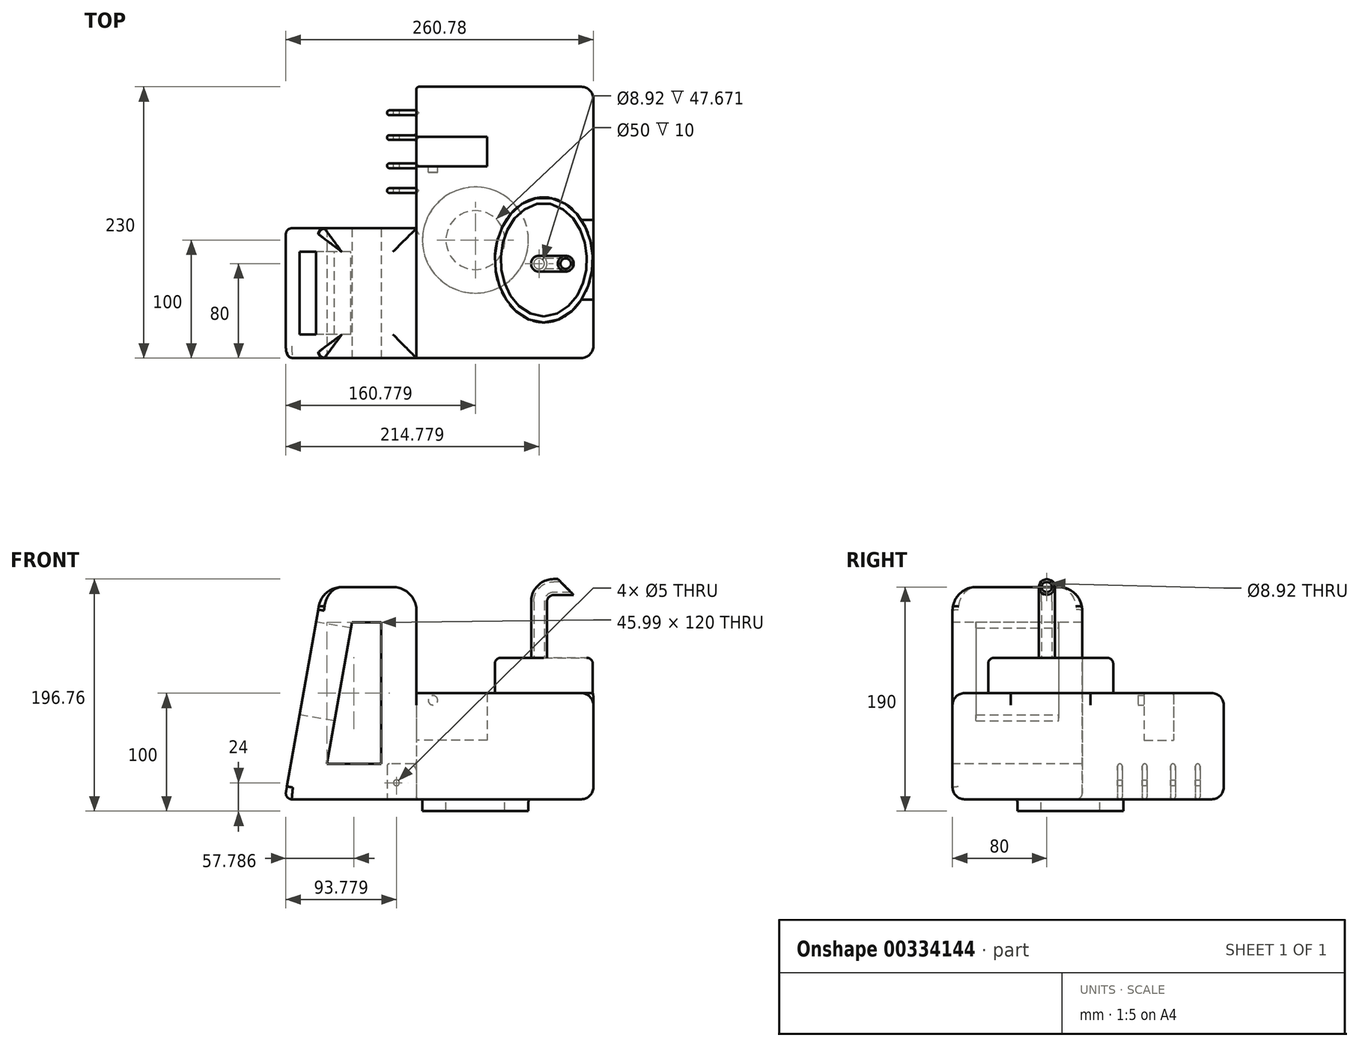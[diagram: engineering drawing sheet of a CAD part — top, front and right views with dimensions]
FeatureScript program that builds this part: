
annotation { "Feature Type Name" : "Feature", "Feature Type Description" : "" }
export const myFeature = defineFeature(function(context is Context, id is Id, definition is map)
    precondition{}
    {
        {
            var Q0;
            Q0=qCreatedBy(makeId("Front.planeOp"),FACE);
            var sketch = newSketch(context, id + "F0", { "sketchPlane" : qUnion([Q0])});
            skLineSegment(sketch, "E0", {"start": v(0, 0) * mm, "end": v(31.74, 180) * mm});
            skLineSegment(sketch, "E1", {"start": v(31.74, 180) * mm, "end": v(111.74, 180) * mm});
            skLineSegment(sketch, "E2", {"start": v(111.74, 180) * mm, "end": v(111.74, 0) * mm});
            skLineSegment(sketch, "E3", {"start": v(111.74, 0) * mm, "end": v(0, 0) * mm});
            skLineSegment(sketch, "E4", {"start": v(111.74, 90) * mm, "end": v(261.74, 90) * mm});
            skLineSegment(sketch, "E5", {"start": v(261.74, 90) * mm, "end": v(261.74, 0) * mm});
            skLineSegment(sketch, "E6", {"start": v(261.74, 0) * mm, "end": v(111.74, 0) * mm});
            skSolve(sketch);
        }
        {
            var Q0;
            {var subQ2=sQuery(id+"F0.wireOp",EDGE,"E4");Q0=makeQuery(id+"F0.imprint","IMPRINT",FACE,{"disambiguationData":[TD([[makeQuery(id+"F0.imprint","IMPRINT",EDGE,{"derivedFrom":subQ2}),-1.0]])]});}
            extrude(context, id + "F1", {"entities" : qUnion([Q0]), "oppositeDirection" : true, "depth" : 230 * mm});
        }
        {
            var Q0;
            Q0=makeQuery(id+"F0.imprint","IMPRINT",FACE,{"disambiguationData":[TD([[makeQuery(id+"F0.imprint","IMPRINT",EDGE,{"derivedFrom":sQuery(id+"F0.wireOp",EDGE,"E0")}),-1.0]])]});
            extrude(context, id + "F2", {"entities" : qUnion([Q0]), "operationType" : NewBodyOperationType.ADD, "oppositeDirection" : true, "depth" : 110 * mm});
        }
        {
            var Q0;
            Q0=makeQuery(id+"F2.boolean.opBoolean","MERGE",FACE,{"derivedFrom":[makeQuery(id+"F1.opExtrude","SWEPT_FACE",FACE,{"disambiguationData":[OSD([sQuery(id+"F0.wireOp",EDGE,"E6")])]}),makeQuery(id+"F2.opExtrude","SWEPT_FACE",FACE,{"disambiguationData":[OSD([sQuery(id+"F0.wireOp",EDGE,"E3")])]})]});
            var sketch = newSketch(context, id + "F3", { "sketchPlane" : qUnion([Q0])});
            skCircle(sketch, "E7", {"center": v(161.74, -100) * mm, "radius": 45 * mm});
            skCircle(sketch, "E8", {"center": v(161.74, -100) * mm, "radius": 25 * mm});
            skSolve(sketch);
        }
        {
            var Q0;
            Q0 = qSketchRegion(id + "F3", true);
            extrude(context, id + "F4", {"entities" : qUnion([Q0]), "operationType" : NewBodyOperationType.ADD, "depth" : 10 * mm});
        }
        {
            var Q0;
            Q0=makeQuery(id+"F0.imprint","IMPRINT",FACE,{"disambiguationData":[TD([[makeQuery(id+"F0.imprint","IMPRINT",EDGE,{"derivedFrom":sQuery(id+"F0.wireOp",EDGE,"E0")}),-1.0]])]});
            var sketch = newSketch(context, id + "F5", { "sketchPlane" : qUnion([Q0])});
            skLineSegment(sketch, "E9.0", {"start": v(81.74, 50) * mm, "end": v(81.74, 150) * mm});
            skLineSegment(sketch, "E9.1", {"start": v(81.74, 30) * mm, "end": v(81.74, 50) * mm});
            skLineSegment(sketch, "E9.2", {"start": v(81.74, 150) * mm, "end": v(56.91, 150) * mm});
            skLineSegment(sketch, "E9.3", {"start": v(56.91, 150) * mm, "end": v(35.75, 30) * mm});
            skLineSegment(sketch, "E9.4", {"start": v(35.75, 30) * mm, "end": v(81.74, 30) * mm});
            skSolve(sketch);
        }
        {
            var Q0;
            Q0 = qSketchRegion(id + "F5", true);
            extrude(context, id + "F6", {"entities" : qUnion([Q0]), "operationType" : NewBodyOperationType.REMOVE, "endBound" : BoundingType.THROUGH_ALL, "oppositeDirection" : true, "depth" : 25 * mm});
        }
        {
            var Q0;
            Q0=makeQuery(id+"F1.opExtrude","SWEPT_FACE",FACE,{"disambiguationData":[OSD([sQuery(id+"F0.wireOp",EDGE,"E2")])]});
            var sketch = newSketch(context, id + "F7", { "sketchPlane" : qUnion([Q0])});
            skLineSegment(sketch, "E10.bottom", {"start": v(-140, 30) * mm, "end": v(-144, 30) * mm});
            skLineSegment(sketch, "E10.top", {"start": v(-140, 0) * mm, "end": v(-144, 0) * mm});
            skLineSegment(sketch, "E10.left", {"start": v(-140, 30) * mm, "end": v(-140, 0) * mm});
            skLineSegment(sketch, "E10.right", {"start": v(-210, 30) * mm, "end": v(-210, 0) * mm});
            skPoint(sketch, "E10.middle", {"position": v(-175, 15) * mm});
            skLineSegment(sketch, "E11", {"start": v(-185, 30) * mm, "end": v(-185, 0) * mm});
            skLineSegment(sketch, "E12", {"start": v(-165, 30) * mm, "end": v(-165, 0) * mm});
            skLineSegment(sketch, "E13", {"start": v(-175, 98.41) * mm, "end": v(-175, -73.6) * mm, "construction": true});
            skLineSegment(sketch, "E14.trimOffspring", {"start": v(-185, 30) * mm, "end": v(-189, 30) * mm});
            skLineSegment(sketch, "E15.trimOffspring", {"start": v(-185, 0) * mm, "end": v(-189, 0) * mm});
            skPoint(sketch, "E16.centerSnap0", {"position": v(-197.5, 30) * mm});
            skPoint(sketch, "E16.centerSnap1", {"position": v(-210, 15) * mm});
            skLineSegment(sketch, "E17", {"start": v(-206, 30) * mm, "end": v(-206, 0) * mm});
            skLineSegment(sketch, "E18", {"start": v(-189, 30) * mm, "end": v(-189, 0) * mm});
            skLineSegment(sketch, "E19.MirrorCS", {"start": v(-161, 30) * mm, "end": v(-161, 0) * mm});
            skLineSegment(sketch, "E20.MirrorCS", {"start": v(-144, 30) * mm, "end": v(-144, 0) * mm});
            skLineSegment(sketch, "E21.trimOffspring", {"start": v(-206, 30) * mm, "end": v(-210, 30) * mm});
            skLineSegment(sketch, "E22.trimOffspring", {"start": v(-206, 0) * mm, "end": v(-210, 0) * mm});
            skLineSegment(sketch, "E23.trimOffspring", {"start": v(-161, 30) * mm, "end": v(-165, 30) * mm});
            skLineSegment(sketch, "E24.trimOffspring", {"start": v(-161, 0) * mm, "end": v(-165, 0) * mm});
            skSolve(sketch);
        }
        {
            var Q0;
            Q0 = qSketchRegion(id + "F7", true);
            extrude(context, id + "F8", {"entities" : qUnion([Q0]), "operationType" : NewBodyOperationType.ADD, "depth" : 25 * mm});
        }
        {
            var Q0;
            {var subQ2=sQuery(id+"F0.wireOp",EDGE,"E4");var subQ3=sQuery(id+"F0.wireOp",EDGE,"E2");Q0=makeQuery(id+"F8.boolean.opBoolean","SPLIT",FACE,{"disambiguationData":[TD([makeQuery(id+"F1.opExtrude","SWEPT_FACE",FACE,{"disambiguationData":[OSD([subQ2])]})])],"derivedFrom":makeQuery(id+"F1.opExtrude","SWEPT_FACE",FACE,{"disambiguationData":[OSD([subQ3])]})});}
            var sketch = newSketch(context, id + "F9", { "sketchPlane" : qUnion([Q0])});
            skLineSegment(sketch, "E25.top", {"start": v(-162.5, 50) * mm, "end": v(-187.5, 50) * mm});
            skLineSegment(sketch, "E25.left", {"start": v(-162.5, 90) * mm, "end": v(-162.5, 50) * mm});
            skLineSegment(sketch, "E25.right", {"start": v(-187.5, 90) * mm, "end": v(-187.5, 50) * mm});
            skPoint(sketch, "E25.middle", {"position": v(-175, 55) * mm});
            skPoint(sketch, "E26.orphan", {"position": v(-187.5, 60) * mm});
            skPoint(sketch, "E27.orphan", {"position": v(-162.5, 60) * mm});
            skLineSegment(sketch, "E28.0", {"start": v(-187.5, 90) * mm, "end": v(-162.5, 90) * mm});
            skPoint(sketch, "E29.orphan", {"position": v(-230, 90) * mm});
            skPoint(sketch, "E30.orphan", {"position": v(-110, 90) * mm});
            skSolve(sketch);
        }
        {
            var Q0;
            Q0=makeQuery(id+"F9.imprint","IMPRINT",FACE,{"disambiguationData":[TD([[makeQuery(id+"F9.imprint","IMPRINT",EDGE,{"derivedFrom":sQuery(id+"F9.wireOp",EDGE,"E25.top")}),-1.0]])]});
            var Q1;
            Q1 = qConstructionFilter(qBodyType(qCreatedBy(id + "F9" ,EDGE), BodyType.WIRE), ConstructionObject.NO);
            extrude(context, id + "F10", {"entities" : qUnion([Q0]), "operationType" : NewBodyOperationType.REMOVE, "surfaceEntities" : qUnion([Q1]), "oppositeDirection" : true, "depth" : 60 * mm});
        }
        {
            var Q0;
            Q0=makeQuery(id+"F10.boolean.opBoolean","COPY",FACE,{"derivedFrom":makeQuery(id+"F10.opExtrude","SWEPT_FACE",FACE,{"disambiguationData":[OSD([sQuery(id+"F9.wireOp",EDGE,"E25.left")])]})});
            var sketch = newSketch(context, id + "F11", { "sketchPlane" : qUnion([Q0])});
            skCircle(sketch, "E31", {"center": v(-125.74, 84) * mm, "radius": 4 * mm});
            skSolve(sketch);
        }
        {
            var Q0;
            Q0 = qSketchRegion(id + "F11", true);
            extrude(context, id + "F12", {"entities" : qUnion([Q0]), "operationType" : NewBodyOperationType.REMOVE, "oppositeDirection" : true, "depth" : 5 * mm});
        }
        {
            var Q0;
            Q0=makeQuery(id+"F2.opExtrude","SWEPT_FACE",FACE,{"disambiguationData":[OSD([sQuery(id+"F0.wireOp",EDGE,"E0")])]});
            var sketch = newSketch(context, id + "F13", { "sketchPlane" : qUnion([Q0])});
            skLineSegment(sketch, "E32.bottom", {"start": v(-20, 152.78) * mm, "end": v(-90, 152.78) * mm});
            skLineSegment(sketch, "E32.top", {"start": v(-20, 72.78) * mm, "end": v(-90, 72.78) * mm});
            skLineSegment(sketch, "E32.left", {"start": v(-20, 152.78) * mm, "end": v(-20, 72.78) * mm});
            skLineSegment(sketch, "E32.right", {"start": v(-90, 152.78) * mm, "end": v(-90, 72.78) * mm});
            skPoint(sketch, "E32.middle", {"position": v(-55, 112.78) * mm});
            skSolve(sketch);
        }
        {
            var Q0;
            Q0 = qSketchRegion(id + "F13", true);
            extrude(context, id + "F14", {"entities" : qUnion([Q0]), "operationType" : NewBodyOperationType.REMOVE, "oppositeDirection" : true, "depth" : 40 * mm});
        }
        {
            var Q0;
            Q0=makeQuery(id+"F1.opExtrude","SWEPT_FACE",FACE,{"disambiguationData":[OSD([sQuery(id+"F0.wireOp",EDGE,"E4")])]});
            var sketch = newSketch(context, id + "F15", { "sketchPlane" : qUnion([Q0])});
            skEllipse(sketch, "E33", {"center": v(219.74, 83.26) * mm, "majorRadius": 53 * mm, "minorRadius": 41.5 * mm, "majorAxis": v(0, -1)});
            skSolve(sketch);
        }
        {
            var Q0;
            Q0 = qSketchRegion(id + "F15", true);
            extrude(context, id + "F16", {"entities" : qUnion([Q0]), "operationType" : NewBodyOperationType.ADD, "depth" : 30 * mm});
        }
        {
            var Q0;
            Q0=qCreatedBy(makeId("Front.planeOp"),FACE);
            cPlane(context, id + "F17", {"entities" : qUnion([Q0]), "cplaneType" : CPlaneType.OFFSET, "offset" : 80 * mm, "oppositeDirection" : true, "width" : 150 * mm, "height" : 150 * mm});
        }
        {
            var Q0;
            Q0=qCreatedBy(id+"F17.planeOp",FACE);
            var sketch = newSketch(context, id + "F18", { "sketchPlane" : qUnion([Q0])});
            skLineSegment(sketch, "E34", {"start": v(215.74, 120) * mm, "end": v(215.74, 167.67) * mm});
            skLineSegment(sketch, "E35", {"start": v(228.07, 180) * mm, "end": v(245.74, 180) * mm});
            skArc(sketch, "E36", {"start": v(228.07, 180) * mm, "mid": v(219.35, 176.39) * mm, "end": v(215.74, 167.67) * mm});
            skSolve(sketch);
        }
        {
            var Q0;
            Q0=sQuery(id+"F18.wireOp",VERTEX,"E35.end");
            var Q1;
            Q1=sQuery(id+"F18.wireOp",EDGE,"E35");
            cPlane(context, id + "F19", {"entities" : qUnion([Q0, Q1]), "cplaneType" : CPlaneType.CURVE_POINT, "offset" : 25 * mm, "width" : 150 * mm, "height" : 150 * mm});
        }
        {
            var Q0;
            Q0=qCreatedBy(id+"F19.planeOp",FACE);
            var sketch = newSketch(context, id + "F20", { "sketchPlane" : qUnion([Q0])});
            skPoint(sketch, "E37.0", {"position": v(80, 180) * mm});
            skCircle(sketch, "E38", {"center": v(80, 180) * mm, "radius": 6.76 * mm});
            skCircle(sketch, "E39", {"center": v(80, 180) * mm, "radius": 4.46 * mm});
            skSolve(sketch);
        }
        {
            var Q0;
            Q0=makeQuery(id+"F20.imprint","IMPRINT",FACE,{"disambiguationData":[TD([[makeQuery(id+"F20.imprint","IMPRINT",EDGE,{"derivedFrom":sQuery(id+"F20.wireOp",EDGE,"E38")}),1.0]])]});
            var Q1;
            Q1=sQuery(id+"F18.wireOp",EDGE,"E35");
            var Q2;
            Q2=sQuery(id+"F18.wireOp",EDGE,"E36");
            var Q3;
            Q3=sQuery(id+"F18.wireOp",EDGE,"E34");
            sweep(context, id + "F21", {"profiles" : qUnion([Q0]), "path" : qUnion([Q1, Q2, Q3])});
        }
        {
            var Q0;
            Q0=qCreatedBy(id+"F17.planeOp",FACE);
            var sketch = newSketch(context, id + "F22", { "sketchPlane" : qUnion([Q0])});
            skLineSegment(sketch, "E40", {"start": v(245.74, 172.62) * mm, "end": v(231.6, 186.76) * mm});
            skLineSegment(sketch, "E41", {"start": v(231.6, 186.76) * mm, "end": v(245.74, 186.76) * mm});
            skLineSegment(sketch, "E42", {"start": v(231.6, 186.76) * mm, "end": v(265.74, 186.76) * mm});
            skLineSegment(sketch, "E43", {"start": v(265.74, 173.24) * mm, "end": v(248.07, 173.24) * mm});
            skLineSegment(sketch, "E44", {"start": v(245.74, 186.76) * mm, "end": v(245.74, 172.62) * mm});
            skSolve(sketch);
        }
        {
            var Q0;
            Q0 = qSketchRegion(id + "F22", true);
            extrude(context, id + "F23", {"entities" : qUnion([Q0]), "operationType" : NewBodyOperationType.REMOVE, "oppositeDirection" : true, "depth" : 25 * mm, "symmetric" : true});
        }
        {
            var Q0;
            Q0=makeQuery(id+"F1.opExtrude","CAP_EDGE",EDGE,{"disambiguationData":[OSD([sQuery(id+"F0.wireOp",EDGE,"E4")])],"isStart":true});
            var Q1;
            Q1=makeQuery(id+"F1.opExtrude","SWEPT_EDGE",EDGE,{"disambiguationData":[OSD([sQuery(id+"F0.wireOp",EDGE,"E4"),sQuery(id+"F0.wireOp",EDGE,"E5")])]});
            var Q2;
            Q2=makeQuery(id+"F1.opExtrude","CAP_EDGE",EDGE,{"disambiguationData":[OSD([sQuery(id+"F0.wireOp",EDGE,"E4")])],"isStart":false});
            var Q3;
            Q3=makeQuery(id+"F1.opExtrude","SWEPT_EDGE",EDGE,{"disambiguationData":[OSD([sQuery(id+"F0.wireOp",EDGE,"E5"),sQuery(id+"F0.wireOp",EDGE,"E6")])]});
            var Q4;
            Q4=makeQuery(id+"F2.boolean.opBoolean","MERGE",EDGE,{"derivedFrom":[makeQuery(id+"F1.opExtrude","CAP_EDGE",EDGE,{"disambiguationData":[OSD([sQuery(id+"F0.wireOp",EDGE,"E6")])],"isStart":true}),makeQuery(id+"F2.opExtrude","CAP_EDGE",EDGE,{"disambiguationData":[OSD([sQuery(id+"F0.wireOp",EDGE,"E3")])],"isStart":true})]});
            var Q5;
            Q5=makeQuery(id+"F1.opExtrude","CAP_EDGE",EDGE,{"disambiguationData":[OSD([sQuery(id+"F0.wireOp",EDGE,"E5")])],"isStart":false});
            var Q6;
            Q6=makeQuery(id+"F1.opExtrude","CAP_EDGE",EDGE,{"disambiguationData":[OSD([sQuery(id+"F0.wireOp",EDGE,"E6")])],"isStart":false});
            var Q7;
            Q7=makeQuery(id+"F1.opExtrude","CAP_EDGE",EDGE,{"disambiguationData":[OSD([sQuery(id+"F0.wireOp",EDGE,"E5")])],"isStart":true});
            fillet(context, id + "F24", {"entities" : qUnion([Q0, Q1, Q2, Q3, Q4, Q5, Q6, Q7]), "radius" : 10 * mm, "tangentPropagation" : true, "allowEdgeOverflow" : false});
        }
        {
            var Q0;
            Q0=makeQuery(id+"F16.opExtrude","CAP_EDGE",EDGE,{"disambiguationData":[OSD([sQuery(id+"F15.wireOp",EDGE,"E33")])],"isStart":false});
            fillet(context, id + "F25", {"entities" : qUnion([Q0]), "radius" : 5 * mm, "tangentPropagation" : true, "allowEdgeOverflow" : false});
        }
        {
            var Q0;
            Q0=makeQuery(id+"F2.opExtrude","SWEPT_FACE",FACE,{"disambiguationData":[OSD([sQuery(id+"F0.wireOp",EDGE,"E1")])]});
            fillet(context, id + "F26", {"entities" : qUnion([Q0]), "radius" : 20 * mm, "tangentPropagation" : true, "allowEdgeOverflow" : false});
        }
        {
            var Q0;
            Q0=makeQuery(id+"F2.opExtrude","CAP_EDGE",EDGE,{"disambiguationData":[OSD([sQuery(id+"F0.wireOp",EDGE,"E0")])],"isStart":false});
            var Q1;
            Q1=makeQuery(id+"F14.boolean.opBoolean","COPY",EDGE,{"derivedFrom":makeQuery(id+"F14.opExtrude","CAP_EDGE",EDGE,{"disambiguationData":[OSD([sQuery(id+"F13.wireOp",EDGE,"E32.bottom")])],"isStart":true})});
            var Q2;
            Q2=makeQuery(id+"F14.boolean.opBoolean","COPY",EDGE,{"derivedFrom":makeQuery(id+"F14.opExtrude","CAP_EDGE",EDGE,{"disambiguationData":[OSD([sQuery(id+"F13.wireOp",EDGE,"E32.top")])],"isStart":true})});
            fillet(context, id + "F27", {"entities" : qUnion([Q0, Q1, Q2]), "radius" : 5 * mm, "tangentPropagation" : true, "allowEdgeOverflow" : false});
        }
        {
            var Q0;
            Q0=makeQuery(id+"F2.opExtrude","SWEPT_EDGE",EDGE,{"disambiguationData":[OSD([sQuery(id+"F0.wireOp",EDGE,"E0"),sQuery(id+"F0.wireOp",EDGE,"E3")])]});
            fillet(context, id + "F28", {"entities" : qUnion([Q0]), "radius" : 5 * mm, "tangentPropagation" : true, "allowEdgeOverflow" : false});
        }
        {
            var Q0;
            Q0=makeQuery(id+"F10.boolean.opBoolean","COPY",EDGE,{"derivedFrom":makeQuery(id+"F10.opExtrude","SWEPT_EDGE",EDGE,{"disambiguationData":[OSD([sQuery(id+"F0.wireOp",EDGE,"E2"),sQuery(id+"F0.wireOp",EDGE,"E4"),sQuery(id+"F9.wireOp",EDGE,"E25.left"),sQuery(id+"F9.wireOp",EDGE,"E28.0")])]})});
            var Q1;
            Q1=makeQuery(id+"F10.boolean.opBoolean","COPY",EDGE,{"derivedFrom":makeQuery(id+"F10.opExtrude","CAP_EDGE",EDGE,{"disambiguationData":[OSD([sQuery(id+"F9.wireOp",EDGE,"E28.0")])],"isStart":false})});
            var Q2;
            Q2=makeQuery(id+"F10.boolean.opBoolean","COPY",EDGE,{"derivedFrom":makeQuery(id+"F10.opExtrude","SWEPT_EDGE",EDGE,{"disambiguationData":[OSD([sQuery(id+"F0.wireOp",EDGE,"E2"),sQuery(id+"F0.wireOp",EDGE,"E4"),sQuery(id+"F9.wireOp",EDGE,"E25.right"),sQuery(id+"F9.wireOp",EDGE,"E28.0")])]})});
            var Q3;
            Q3=makeQuery(id+"F10.boolean.opBoolean","COPY",EDGE,{"derivedFrom":makeQuery(id+"F10.opExtrude","CAP_EDGE",EDGE,{"disambiguationData":[OSD([sQuery(id+"F9.wireOp",EDGE,"E25.left")])],"isStart":true})});
            var Q4;
            Q4=makeQuery(id+"F10.boolean.opBoolean","COPY",EDGE,{"derivedFrom":makeQuery(id+"F10.opExtrude","CAP_EDGE",EDGE,{"disambiguationData":[OSD([sQuery(id+"F9.wireOp",EDGE,"E25.right")])],"isStart":true})});
            var Q5;
            Q5=makeQuery(id+"F10.boolean.opBoolean","COPY",EDGE,{"derivedFrom":makeQuery(id+"F10.opExtrude","CAP_EDGE",EDGE,{"disambiguationData":[OSD([sQuery(id+"F9.wireOp",EDGE,"E25.top")])],"isStart":true})});
            var Q6;
            Q6=makeQuery(id+"F8.opExtrude","CAP_FACE",FACE,{"disambiguationData":[OSD([sQuery(id+"F7.wireOp",EDGE,"E10.right"),sQuery(id+"F7.wireOp",EDGE,"E17"),sQuery(id+"F7.wireOp",EDGE,"E21.trimOffspring"),sQuery(id+"F7.wireOp",EDGE,"E22.trimOffspring")])],"isStart":false});
            var Q7;
            Q7=makeQuery(id+"F8.opExtrude","SWEPT_FACE",FACE,{"disambiguationData":[OSD([sQuery(id+"F7.wireOp",EDGE,"E21.trimOffspring")])]});
            var Q8;
            {var subQ2=sQuery(id+"F0.wireOp",EDGE,"E6");var subQ4=sQuery(id+"F0.wireOp",EDGE,"E2");var subQ5=sQuery(id+"F0.wireOp",EDGE,"E3");Q8=makeQuery(id+"F8.boolean.opBoolean","MERGE",FACE,{"derivedFrom":[makeQuery(id+"F4.boolean.opBoolean","SPLIT",FACE,{"disambiguationData":[TD([makeQuery(id+"F1.opExtrude","SWEPT_FACE",FACE,{"disambiguationData":[OSD([subQ4])]})])],"derivedFrom":makeQuery(id+"F2.boolean.opBoolean","MERGE",FACE,{"derivedFrom":[makeQuery(id+"F1.opExtrude","SWEPT_FACE",FACE,{"disambiguationData":[OSD([subQ2])]}),makeQuery(id+"F2.opExtrude","SWEPT_FACE",FACE,{"disambiguationData":[OSD([subQ5])]})]})}),makeQuery(id+"F8.opExtrude","SWEPT_FACE",FACE,{"disambiguationData":[OSD([sQuery(id+"F7.wireOp",EDGE,"E10.top")])]}),makeQuery(id+"F8.opExtrude","SWEPT_FACE",FACE,{"disambiguationData":[OSD([sQuery(id+"F7.wireOp",EDGE,"E15.trimOffspring")])]}),makeQuery(id+"F8.opExtrude","SWEPT_FACE",FACE,{"disambiguationData":[OSD([sQuery(id+"F7.wireOp",EDGE,"E22.trimOffspring")])]}),makeQuery(id+"F8.opExtrude","SWEPT_FACE",FACE,{"disambiguationData":[OSD([sQuery(id+"F7.wireOp",EDGE,"E24.trimOffspring")])]})]});}
            var Q9;
            Q9=makeQuery(id+"F8.opExtrude","CAP_FACE",FACE,{"disambiguationData":[OSD([sQuery(id+"F7.wireOp",EDGE,"E11"),sQuery(id+"F7.wireOp",EDGE,"E14.trimOffspring"),sQuery(id+"F7.wireOp",EDGE,"E15.trimOffspring"),sQuery(id+"F7.wireOp",EDGE,"E18")])],"isStart":false});
            var Q10;
            Q10=makeQuery(id+"F8.opExtrude","CAP_EDGE",EDGE,{"disambiguationData":[OSD([sQuery(id+"F7.wireOp",EDGE,"E19.MirrorCS")])],"isStart":false});
            var Q11;
            Q11=makeQuery(id+"F8.opExtrude","CAP_EDGE",EDGE,{"disambiguationData":[OSD([sQuery(id+"F7.wireOp",EDGE,"E12")])],"isStart":false});
            var Q12;
            Q12=makeQuery(id+"F8.opExtrude","CAP_FACE",FACE,{"disambiguationData":[OSD([sQuery(id+"F7.wireOp",EDGE,"E10.bottom"),sQuery(id+"F7.wireOp",EDGE,"E10.top"),sQuery(id+"F7.wireOp",EDGE,"E10.left"),sQuery(id+"F7.wireOp",EDGE,"E20.MirrorCS")])],"isStart":false});
            var Q13;
            Q13=makeQuery(id+"F8.opExtrude","SWEPT_FACE",FACE,{"disambiguationData":[OSD([sQuery(id+"F7.wireOp",EDGE,"E10.bottom")])]});
            var Q14;
            Q14=makeQuery(id+"F8.opExtrude","SWEPT_FACE",FACE,{"disambiguationData":[OSD([sQuery(id+"F7.wireOp",EDGE,"E23.trimOffspring")])]});
            var Q15;
            Q15=makeQuery(id+"F8.opExtrude","SWEPT_FACE",FACE,{"disambiguationData":[OSD([sQuery(id+"F7.wireOp",EDGE,"E14.trimOffspring")])]});
            fillet(context, id + "F29", {"entities" : qUnion([Q0, Q1, Q2, Q3, Q4, Q5, Q6, Q7, Q8, Q9, Q10, Q11, Q12, Q13, Q14, Q15]), "radius" : 2 * mm, "tangentPropagation" : true, "allowEdgeOverflow" : false});
        }
        {
            var Q0;
            Q0=makeQuery(id+"F8.opExtrude","SWEPT_FACE",FACE,{"disambiguationData":[OSD([sQuery(id+"F7.wireOp",EDGE,"E10.right")])]});
            var sketch = newSketch(context, id + "F30", { "sketchPlane" : qUnion([Q0])});
            skCircle(sketch, "E45", {"center": v(-94.74, 14) * mm, "radius": 2.5 * mm});
            skSolve(sketch);
        }
        {
            var Q0;
            Q0 = qSketchRegion(id + "F30", true);
            var Q1;
            Q1=makeQuery(id+"F8.opExtrude","SWEPT_FACE",FACE,{"disambiguationData":[OSD([sQuery(id+"F7.wireOp",EDGE,"E10.left")])]});
            extrude(context, id + "F31", {"entities" : qUnion([Q0]), "operationType" : NewBodyOperationType.REMOVE, "endBound" : BoundingType.UP_TO_SURFACE, "oppositeDirection" : true, "endBoundEntityFace" : qUnion([Q1]), "depth" : 25 * mm});
        }
        {
            var Q0;
            Q0=qCreatedBy(id+"F17.planeOp",FACE);
            var sketch = newSketch(context, id + "F32", { "sketchPlane" : qUnion([Q0])});
            skLineSegment(sketch, "E46", {"start": v(232.22, 186.76) * mm, "end": v(245.74, 186.76) * mm});
            skLineSegment(sketch, "E47", {"start": v(245.74, 173.24) * mm, "end": v(232.22, 186.76) * mm});
            skLineSegment(sketch, "E48", {"start": v(245.74, 173.24) * mm, "end": v(245.74, 186.76) * mm});
            skSolve(sketch);
        }
        {
            var Q0;
            Q0 = qSketchRegion(id + "F32", true);
            extrude(context, id + "F33", {"entities" : qUnion([Q0]), "operationType" : NewBodyOperationType.REMOVE, "oppositeDirection" : true, "depth" : 25 * mm, "symmetric" : true});
        }
    });
